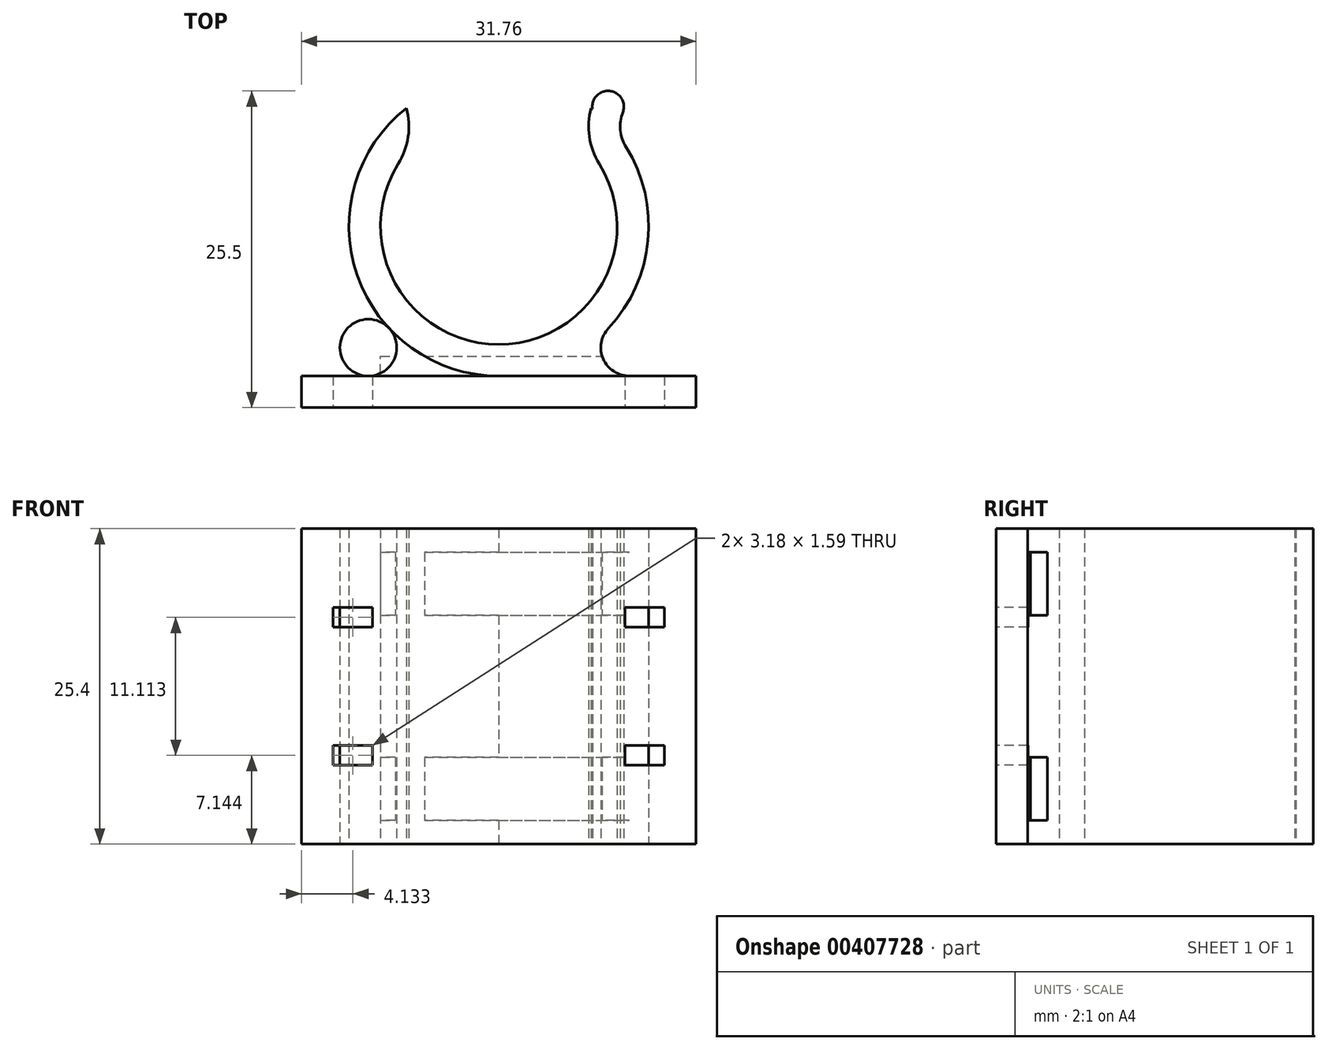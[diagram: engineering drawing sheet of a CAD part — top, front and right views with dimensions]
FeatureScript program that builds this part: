
annotation { "Feature Type Name" : "Feature", "Feature Type Description" : "" }
export const myFeature = defineFeature(function(context is Context, id is Id, definition is map)
    precondition{}
    {
        {
            var Q0;
            Q0=qCreatedBy(makeId("Top.planeOp"),FACE);
            var sketch = newSketch(context, id + "F0", { "sketchPlane" : qUnion([Q0])});
            skCircle(sketch, "E0", {"center": v(0, 0) * mm, "radius": 9.53 * mm});
            skCircle(sketch, "E1.0", {"center": v(0, 0) * mm, "radius": 12.07 * mm});
            skLineSegment(sketch, "E2", {"start": v(0, -12.07) * mm, "end": v(15.88, -12.07) * mm});
            skLineSegment(sketch, "E3", {"start": v(15.88, -12.07) * mm, "end": v(15.88, -14.6) * mm});
            skLineSegment(sketch, "E4", {"start": v(15.88, -14.6) * mm, "end": v(0, -14.6) * mm});
            skPoint(sketch, "E5.orphan", {"position": v(0, -12.07) * mm});
            skCircle(sketch, "E6", {"center": v(10.5, -9.78) * mm, "radius": 2.29 * mm});
            skLineSegment(sketch, "E7.MirrorCS", {"start": v(-15.88, -14.6) * mm, "end": v(0, -14.6) * mm});
            skLineSegment(sketch, "E8.MirrorCS", {"start": v(-15.88, -12.07) * mm, "end": v(-15.88, -14.6) * mm});
            skLineSegment(sketch, "E9.MirrorCS", {"start": v(0, -12.07) * mm, "end": v(-15.88, -12.07) * mm});
            skCircle(sketch, "E10.MirrorC", {"center": v(-10.5, -9.78) * mm, "radius": 2.29 * mm});
            skArc(sketch, "E11", {"start": v(9.98, 9.17) * mm, "mid": v(9.79, 7.74) * mm, "end": v(10.25, 6.37) * mm});
            skArc(sketch, "E12.0", {"start": v(7.6, 10.08) * mm, "mid": v(7.26, 7.5) * mm, "end": v(8.1, 5.03) * mm});
            skArc(sketch, "E13", {"start": v(9.98, 9.17) * mm, "mid": v(8.92, 10.89) * mm, "end": v(7.54, 9.42) * mm});
            skArc(sketch, "E14.MirrorCS", {"start": v(-9.98, 9.17) * mm, "mid": v(-9.79, 7.74) * mm, "end": v(-10.25, 6.37) * mm});
            skArc(sketch, "E15.MirrorCS", {"start": v(-9.98, 9.17) * mm, "mid": v(-8.92, 10.89) * mm, "end": v(-7.54, 9.42) * mm});
            skArc(sketch, "E16.MirrorCS", {"start": v(-7.6, 10.08) * mm, "mid": v(-7.26, 7.5) * mm, "end": v(-8.1, 5.03) * mm});
            skSolve(sketch);
        }
        {
            var Q0;
            {var subQ1=sQuery(id+"F0.wireOp",EDGE,"E1.0");var subQ3=sQuery(id+"F0.wireOp",EDGE,"E6");var subQ4=makeQuery(id+"F0.imprint","INTERSECT",VERTEX,{"derivedFrom":[subQ1,subQ3]});Q0=makeQuery(id+"F0.imprint","IMPRINT",FACE,{"disambiguationData":[TD([[makeQuery(id+"F0.imprint","IMPRINT",EDGE,{"disambiguationData":[TD([[subQ4,-1.0]])],"derivedFrom":subQ3}),-1.0]])]});}
            var Q1;
            {var subQ0=sQuery(id+"F0.wireOp",EDGE,"E3");Q1=makeQuery(id+"F0.imprint","IMPRINT",FACE,{"disambiguationData":[TD([[makeQuery(id+"F0.imprint","IMPRINT",EDGE,{"derivedFrom":subQ0}),-1.0]])]});}
            var Q2;
            {var subQ1=sQuery(id+"F0.wireOp",EDGE,"E1.0");var subQ3=sQuery(id+"F0.wireOp",EDGE,"E10.MirrorC");var subQ4=makeQuery(id+"F0.imprint","INTERSECT",VERTEX,{"derivedFrom":[subQ1,subQ3]});Q2=makeQuery(id+"F0.imprint","IMPRINT",FACE,{"disambiguationData":[TD([[makeQuery(id+"F0.imprint","IMPRINT",EDGE,{"disambiguationData":[TD([[subQ4,-1.0]])],"derivedFrom":subQ3}),1.0]])]});}
            var Q3;
            {var subQ5=sQuery(id+"F0.wireOp",EDGE,"E0");var subQ11=sQuery(id+"F0.wireOp",EDGE,"E12.0");var subQ12=makeQuery(id+"F0.imprint","INTERSECT",VERTEX,{"derivedFrom":[subQ5,subQ11]});Q3=makeQuery(id+"F0.imprint","IMPRINT",FACE,{"disambiguationData":[TD([[makeQuery(id+"F0.imprint","IMPRINT",EDGE,{"disambiguationData":[TD([[subQ12,1.0]])],"derivedFrom":subQ5}),-1.0]])]});}
            var Q4;
            {var subQ0=sQuery(id+"F0.wireOp",EDGE,"E11");Q4=makeQuery(id+"F0.imprint","IMPRINT",FACE,{"disambiguationData":[TD([[makeQuery(id+"F0.imprint","IMPRINT",EDGE,{"derivedFrom":subQ0}),-1.0]])]});}
            var Q5;
            {var subQ0=sQuery(id+"F0.wireOp",EDGE,"E14.MirrorCS");Q5=makeQuery(id+"F0.imprint","IMPRINT",FACE,{"disambiguationData":[TD([[makeQuery(id+"F0.imprint","IMPRINT",EDGE,{"derivedFrom":subQ0}),1.0]])]});}
            extrude(context, id + "F1", {"entities" : qUnion([Q0, Q1, Q2, Q3, Q4, Q5]), "depth" : 25.4 * mm, "offsetDistance" : 25.4 * mm});
        }
        {
            var Q0;
            Q0=makeQuery(id+"F1.opExtrude","SWEPT_FACE",FACE,{"disambiguationData":[OSD([sQuery(id+"F0.wireOp",EDGE,"E4"),sQuery(id+"F0.wireOp",EDGE,"E7.MirrorCS")])]});
            var sketch = newSketch(context, id + "F2", { "sketchPlane" : qUnion([Q0])});
            skLineSegment(sketch, "E17", {"start": v(-15.87, 12.7) * mm, "end": v(15.88, 12.7) * mm, "construction": true});
            skLineSegment(sketch, "E18.bottom", {"start": v(-13.34, 19.05) * mm, "end": v(-10.16, 19.05) * mm});
            skLineSegment(sketch, "E18.top", {"start": v(-13.34, 17.46) * mm, "end": v(-10.16, 17.46) * mm});
            skLineSegment(sketch, "E18.left", {"start": v(-13.34, 19.05) * mm, "end": v(-13.34, 17.46) * mm});
            skLineSegment(sketch, "E18.right", {"start": v(-10.16, 19.05) * mm, "end": v(-10.16, 17.46) * mm});
            skLineSegment(sketch, "E19.MirrorCS", {"start": v(13.34, 19.05) * mm, "end": v(13.34, 17.46) * mm});
            skLineSegment(sketch, "E20.MirrorCS", {"start": v(10.16, 19.05) * mm, "end": v(10.16, 17.46) * mm});
            skLineSegment(sketch, "E21.MirrorCS", {"start": v(13.34, 19.05) * mm, "end": v(10.16, 19.05) * mm});
            skLineSegment(sketch, "E22.MirrorCS", {"start": v(13.34, 17.46) * mm, "end": v(10.16, 17.46) * mm});
            skLineSegment(sketch, "E23.MirrorCS", {"start": v(10.16, 6.35) * mm, "end": v(10.16, 7.94) * mm});
            skLineSegment(sketch, "E24.MirrorCS", {"start": v(13.34, 6.35) * mm, "end": v(13.34, 7.94) * mm});
            skLineSegment(sketch, "E25.MirrorCS", {"start": v(-10.16, 6.35) * mm, "end": v(-10.16, 7.94) * mm});
            skLineSegment(sketch, "E26.MirrorCS", {"start": v(-13.33, 6.35) * mm, "end": v(-13.33, 7.94) * mm});
            skLineSegment(sketch, "E27.MirrorCS", {"start": v(-13.34, 7.94) * mm, "end": v(-10.16, 7.94) * mm});
            skLineSegment(sketch, "E28.MirrorCS", {"start": v(-13.34, 6.35) * mm, "end": v(-10.16, 6.35) * mm});
            skLineSegment(sketch, "E29.MirrorCS", {"start": v(13.34, 6.35) * mm, "end": v(10.16, 6.35) * mm});
            skLineSegment(sketch, "E30.MirrorCS", {"start": v(13.34, 7.94) * mm, "end": v(10.16, 7.94) * mm});
            skSolve(sketch);
        }
        {
            var Q0;
            Q0 = qSketchRegion(id + "F2", true);
            extrude(context, id + "F3", {"entities" : qUnion([Q0]), "operationType" : NewBodyOperationType.REMOVE, "endBound" : BoundingType.UP_TO_NEXT, "oppositeDirection" : true, "depth" : 25.4 * mm, "offsetDistance" : 25.4 * mm});
        }
        {
            var Q0;
            Q0=makeQuery(id+"F1.opExtrude","SWEPT_FACE",FACE,{"disambiguationData":[OSD([sQuery(id+"F0.wireOp",EDGE,"E3")])]});
            var sketch = newSketch(context, id + "F4", { "sketchPlane" : qUnion([Q0])});
            skLineSegment(sketch, "E31.bottom", {"start": v(-12.07, 1.9) * mm, "end": v(-10.48, 1.9) * mm});
            skLineSegment(sketch, "E31.top", {"start": v(-12.07, 6.99) * mm, "end": v(-10.48, 6.99) * mm});
            skLineSegment(sketch, "E31.left", {"start": v(-12.07, 1.9) * mm, "end": v(-12.07, 6.99) * mm});
            skLineSegment(sketch, "E31.right", {"start": v(-10.48, 1.9) * mm, "end": v(-10.48, 6.99) * mm});
            skLineSegment(sketch, "E32", {"start": v(-14.6, 12.7) * mm, "end": v(15.35, 12.7) * mm, "construction": true});
            skPoint(sketch, "E32.endSnap0", {"position": v(-12.07, 12.7) * mm});
            skLineSegment(sketch, "E33.MirrorCS", {"start": v(-10.48, 23.5) * mm, "end": v(-10.48, 18.42) * mm});
            skLineSegment(sketch, "E34.MirrorCS", {"start": v(-12.07, 23.5) * mm, "end": v(-12.07, 18.42) * mm});
            skLineSegment(sketch, "E35.MirrorCS", {"start": v(-12.07, 18.42) * mm, "end": v(-10.48, 18.42) * mm});
            skLineSegment(sketch, "E36.MirrorCS", {"start": v(-12.07, 23.5) * mm, "end": v(-10.48, 23.5) * mm});
            skSolve(sketch);
        }
        {
            var Q0;
            Q0 = qSketchRegion(id + "F4", true);
            extrude(context, id + "F5", {"entities" : qUnion([Q0]), "operationType" : NewBodyOperationType.REMOVE, "oppositeDirection" : true, "depth" : 25.4 * mm, "offsetDistance" : 25.4 * mm});
        }
    });
